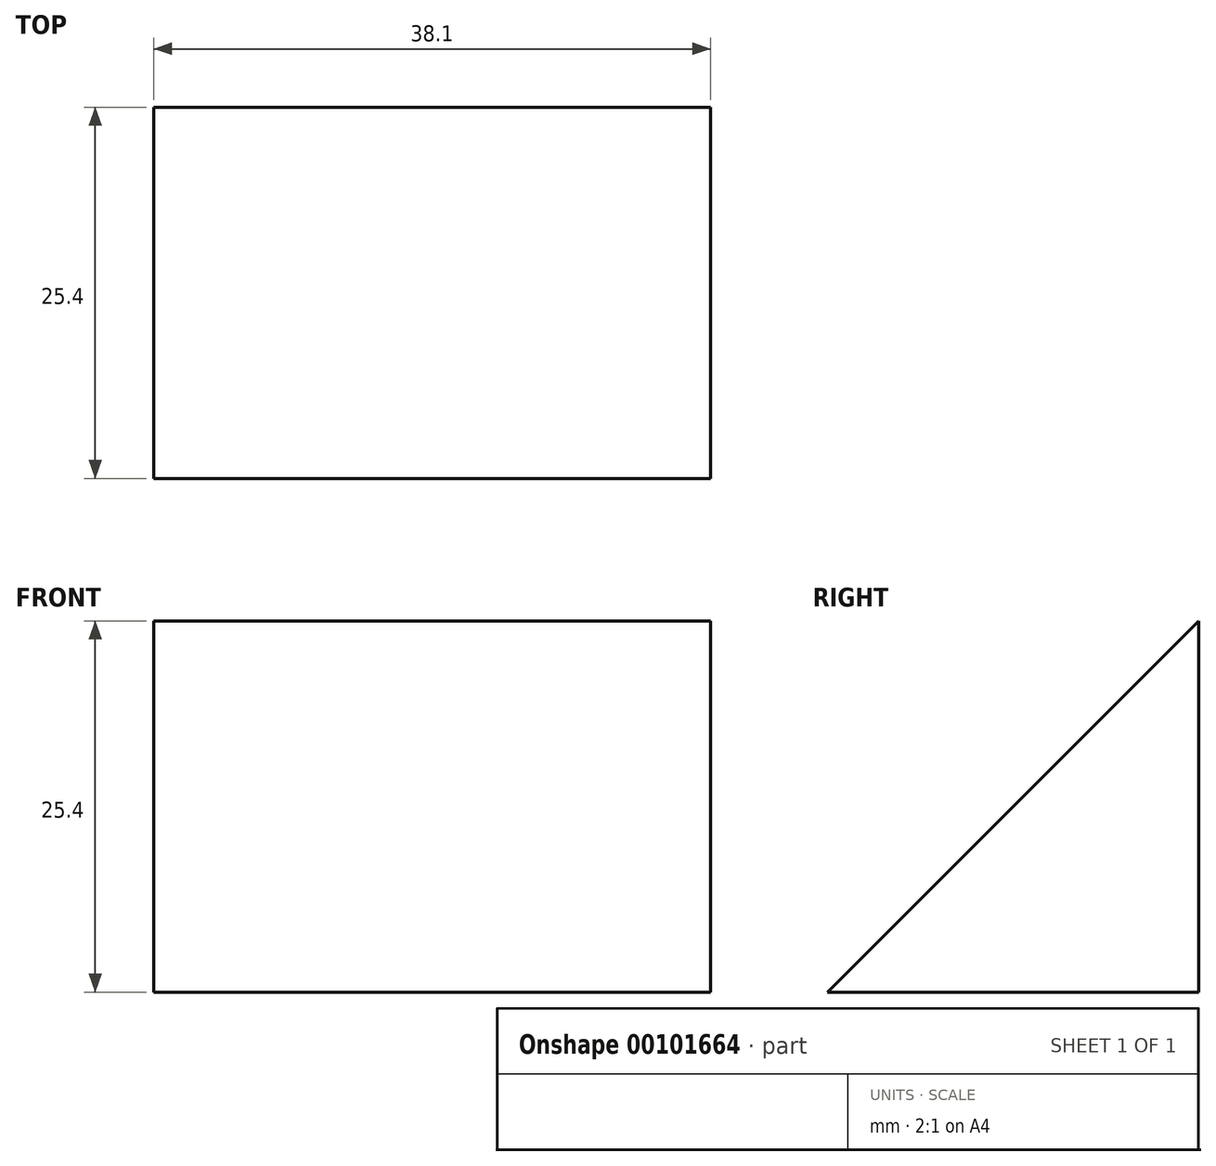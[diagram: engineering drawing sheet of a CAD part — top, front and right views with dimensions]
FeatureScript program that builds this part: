
annotation { "Feature Type Name" : "Feature", "Feature Type Description" : "" }
export const myFeature = defineFeature(function(context is Context, id is Id, definition is map)
    precondition{}
    {
        {
            var Q0;
            Q0=qCreatedBy(makeId("Right.planeOp"),FACE);
            var sketch = newSketch(context, id + "F0", { "sketchPlane" : qUnion([Q0])});
            skLineSegment(sketch, "E0", {"start": v(0, 0) * mm, "end": v(0, 25.4) * mm});
            skLineSegment(sketch, "E1", {"start": v(0, 25.4) * mm, "end": v(-25.4, 0) * mm});
            skLineSegment(sketch, "E2", {"start": v(-25.4, 0) * mm, "end": v(0, 0) * mm});
            skSolve(sketch);
        }
        {
            var Q0;
            Q0 = qSketchRegion(id + "F0", true);
            extrude(context, id + "F1", {"entities" : qUnion([Q0]), "oppositeDirection" : true, "depth" : 38.1 * mm});
        }
    });
